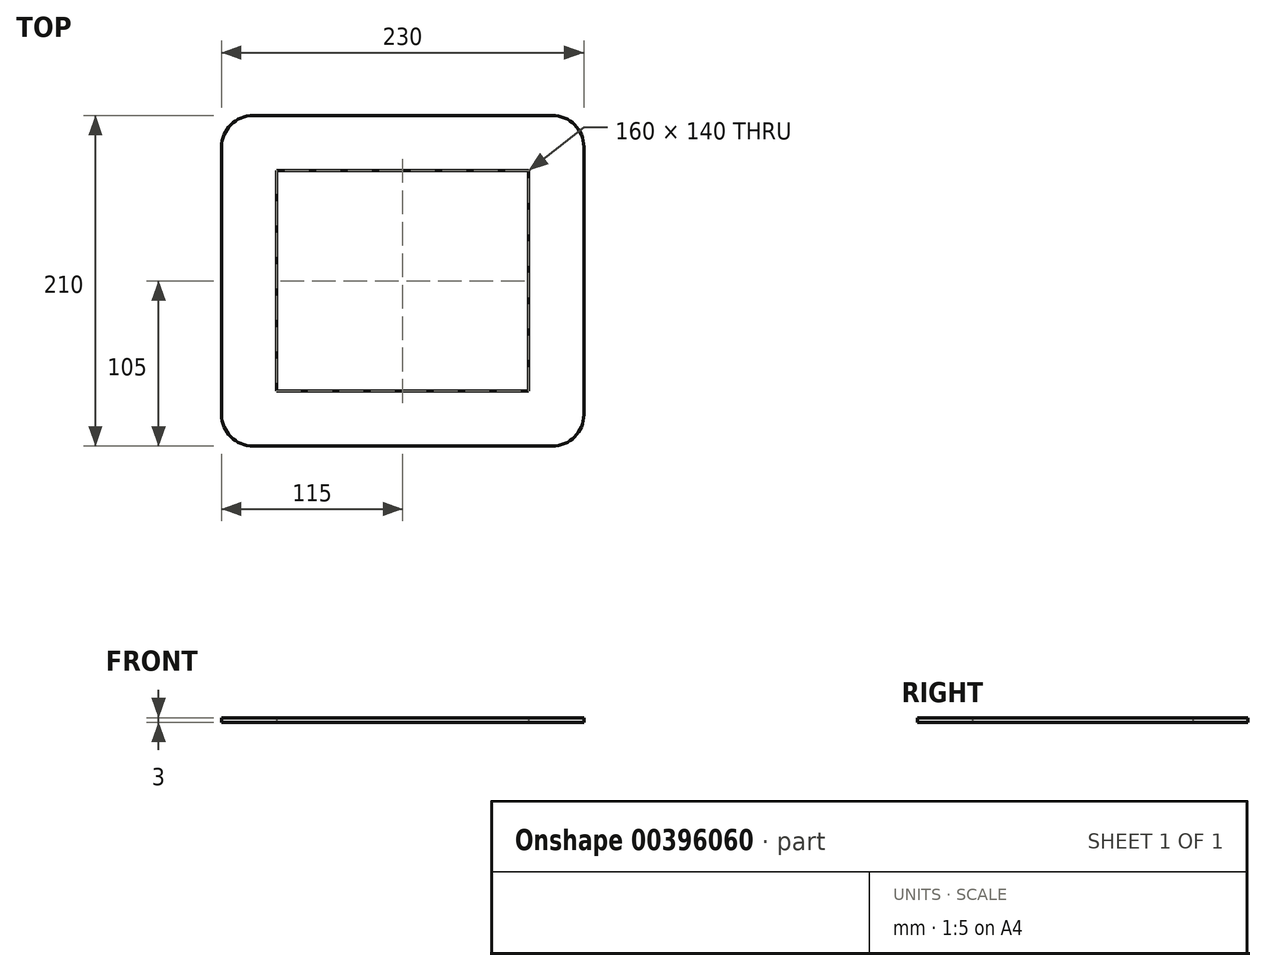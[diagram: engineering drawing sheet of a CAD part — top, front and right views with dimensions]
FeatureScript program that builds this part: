
annotation { "Feature Type Name" : "Feature", "Feature Type Description" : "" }
export const myFeature = defineFeature(function(context is Context, id is Id, definition is map)
    precondition{}
    {
        {
            var Q0;
            Q0=qCreatedBy(makeId("Top.planeOp"),FACE);
            var sketch = newSketch(context, id + "F0", { "sketchPlane" : qUnion([Q0])});
            skLineSegment(sketch, "E0.bottom", {"start": v(-95, 105) * mm, "end": v(95, 105) * mm});
            skLineSegment(sketch, "E0.top", {"start": v(-95, -105) * mm, "end": v(95, -105) * mm});
            skLineSegment(sketch, "E0.left", {"start": v(-115, 85) * mm, "end": v(-115, -85) * mm});
            skLineSegment(sketch, "E0.right", {"start": v(115, 85) * mm, "end": v(115, -85) * mm});
            skPoint(sketch, "E0.middle", {"position": v(0, 0) * mm});
            skPoint(sketch, "E1.visualSharp", {"position": v(-115, 105) * mm});
            skArc(sketch, "E1.filletArc", {"start": v(-95, 105) * mm, "mid": v(-109.14, 99.14) * mm, "end": v(-115, 85) * mm});
            skPoint(sketch, "E2.visualSharp", {"position": v(-115, -105) * mm});
            skArc(sketch, "E2.filletArc", {"start": v(-115, -85) * mm, "mid": v(-109.14, -99.14) * mm, "end": v(-95, -105) * mm});
            skPoint(sketch, "E3.visualSharp", {"position": v(115, -105) * mm});
            skArc(sketch, "E3.filletArc", {"start": v(95, -105) * mm, "mid": v(109.14, -99.14) * mm, "end": v(115, -85) * mm});
            skPoint(sketch, "E4.visualSharp", {"position": v(115, 105) * mm});
            skArc(sketch, "E4.filletArc", {"start": v(115, 85) * mm, "mid": v(109.14, 99.14) * mm, "end": v(95, 105) * mm});
            skLineSegment(sketch, "E5.bottom", {"start": v(-80, 70) * mm, "end": v(80, 70) * mm});
            skLineSegment(sketch, "E5.top", {"start": v(-80, -70) * mm, "end": v(80, -70) * mm});
            skLineSegment(sketch, "E5.left", {"start": v(-80, 70) * mm, "end": v(-80, -70) * mm});
            skLineSegment(sketch, "E5.right", {"start": v(80, 70) * mm, "end": v(80, -70) * mm});
            skSolve(sketch);
        }
        {
            var Q0;
            Q0=qSketchRegion(id+"F0",true);
            extrude(context, id + "F1", {"entities" : qUnion([Q0]), "depth" : 3 * mm});
        }
    });
